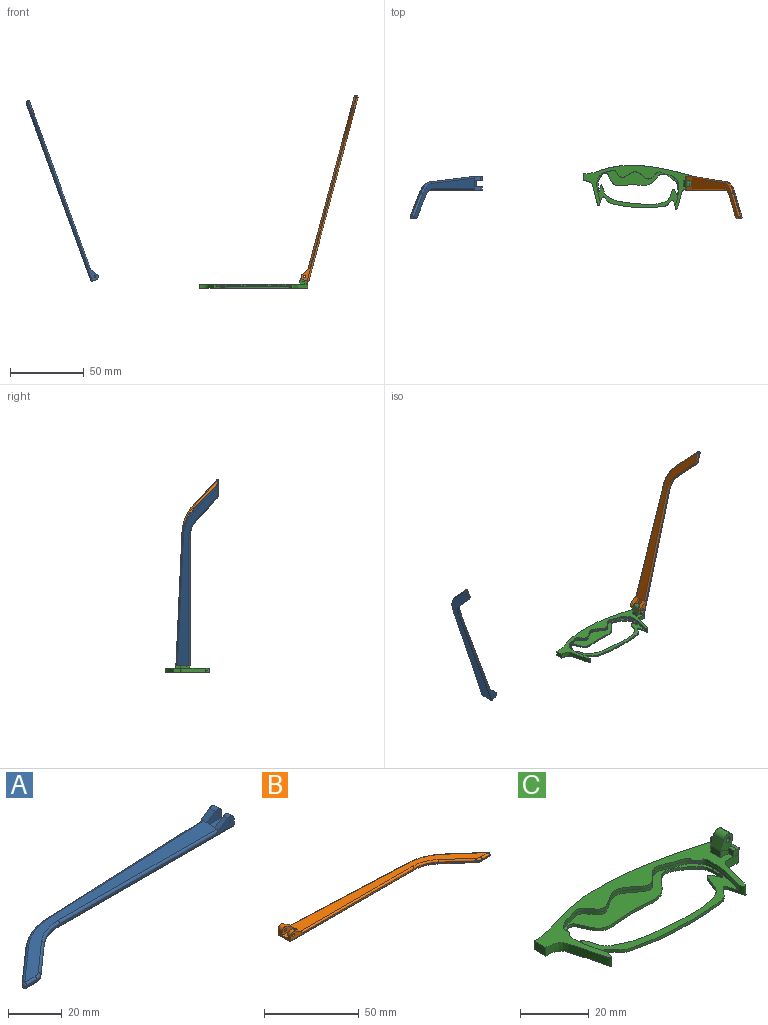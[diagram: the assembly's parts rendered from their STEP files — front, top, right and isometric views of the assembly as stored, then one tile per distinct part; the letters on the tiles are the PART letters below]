
ASSEMBLY  parts=3 mates=1
PART A: 43 faces, bbox 130.2x29.5x5.9 mm
  f0: plane 9.62x3.72mm, normal (1,0,0), area 24.7mm2, adj f1,f3,f4,f5,f10,f16,f18,f28
  f1: cylinder r=2.2mm len=3.45mm, axis (0,-1,0), area 11mm2, adj f0,f2,f4,f37
  f2: plane 6.01x3.91mm, normal (-0.55,0,0.84), area 12.7mm2, adj f1,f4,f9,f19,f37
  f3: plane 2.26x0.1mm, normal (0,0,1), area 0.1mm2, adj f0,f5,f18
  f4: plane 92.1x4.9mm, normal (0,-1,0), area 79.9mm2, adj f0,f1,f2,f14,f19,f36,f42
  f5: plane 93.42x4.13mm, normal (-0.04,1,0), area 64.8mm2, adj f0,f3,f11,f15,f17,f27,f28
  f6: plane 17.82x15.72mm, normal (-0.66,0.75,0), area 14.3mm2, adj f11,f12,f25,f30
  f7: plane 5.46x0.6mm, normal (0,-1,0), area 3.3mm2, adj f12,f13,f23,f32
  f8: plane 14.99x13.23mm, normal (0.66,-0.75,0), area 12mm2, adj f13,f14,f21,f34
  f9: plane 121.18x26.73mm, normal (0,0,1), area 627.7mm2, adj f2,f17,f19,f20,f21,f22,f23,f25
  f10: plane 129.1x27.08mm, normal (0,0,-1), area 686.5mm2, adj f0,f28,f29,f30,f32,f33,f34,f35
  f11: cylinder r=30mm len=18.52mm, axis (0,0,-1), area 12.2mm2, adj f5,f6,f26,f29
  f12: cylinder r=1mm len=1.75mm, axis (0,0,-1), area 1.5mm2, adj f6,f7,f24,f31
  f13: cylinder r=5mm len=3.31mm, axis (0,0,-1), area 2.2mm2, adj f7,f8,f22,f33
  f14: cylinder r=20mm len=13.23mm, axis (0,0,1), area 8.7mm2, adj f4,f8,f20,f35
  f15: plane 5.66x0.25mm, normal (0,0,-1), area 0.7mm2, adj f5,f17,f18
  f16: cylinder r=2.2mm len=3.45mm, axis (0,-1,0), area 14.8mm2, adj f0,f17,f18,f38
  f17: plane 6.01x3.91mm, normal (-0.55,0,0.84), area 16.9mm2, adj f5,f9,f15,f16,f18,f27,f38
  f18: plane 7.92x3.3mm, normal (0,1,0), area 15.9mm2, adj f0,f3,f15,f16,f17,f41
  f19: cylinder r=1mm len=84.18mm, axis (-1,0,0), area 131.4mm2, adj f2,f4,f9,f20
  f20: torus R=21mm, axis (0,0,1), area 23.1mm2, adj f9,f14,f19,f21
  f21: cylinder r=1mm len=15.65mm, axis (-0.75,-0.66,0), area 31.4mm2, adj f8,f9,f20,f22
  f22: torus R=4mm, axis (0,0,1), area 5.3mm2, adj f9,f13,f21,f23
  f23: cylinder r=1mm len=5.46mm, axis (-1,0,0), area 8.6mm2, adj f7,f9,f22,f24
  f24: sphere r=1mm, area 2.4mm2, adj f12,f23,f25
  f25: cylinder r=1mm len=18.48mm, axis (0.75,0.66,0), area 37.3mm2, adj f6,f9,f24,f26
  f26: torus R=29mm, axis (0,0,1), area 31.6mm2, adj f9,f11,f25,f27
  f27: cylinder r=1mm len=85.5mm, axis (1,0.04,0), area 133.5mm2, adj f5,f9,f17,f26
  f28: cylinder r=1mm len=93.46mm, axis (-1,-0.04,0), area 146.9mm2, adj f0,f5,f10,f29
  f29: torus R=29mm, axis (0,0,1), area 31.6mm2, adj f10,f11,f28,f30
  f30: cylinder r=1mm len=18.48mm, axis (-0.75,-0.66,0), area 37.3mm2, adj f6,f10,f29,f31
  f31: sphere r=1mm, area 2.4mm2, adj f12,f30,f32
  f32: cylinder r=1mm len=5.46mm, axis (1,0,0), area 8.6mm2, adj f7,f10,f31,f33
  f33: torus R=4mm, axis (0,0,1), area 5.3mm2, adj f10,f13,f32,f34
  f34: cylinder r=1mm len=15.65mm, axis (0.75,0.66,0), area 31.4mm2, adj f8,f10,f33,f35
  f35: torus R=21mm, axis (0,0,1), area 23.1mm2, adj f10,f14,f34,f36
  f36: cylinder r=1mm len=92.1mm, axis (1,0,0), area 144.7mm2, adj f0,f4,f10,f35
  f37: plane 7.92x4.7mm, normal (0,1,0), area 27mm2, adj f0,f1,f2,f39,f40,f42
  f38: plane 7.92x4.7mm, normal (0,-1,0), area 27mm2, adj f0,f16,f17,f39,f40,f41
  f39: plane 7.92x4.1mm, normal (0,0,1), area 32.5mm2, adj f0,f37,f38,f40
  f40: plane 4.1x1.4mm, normal (1,0,0), area 5.7mm2, adj f9,f37,f38,f39
  f41: cylinder r=0.5mm len=3.1mm, axis (0,-1,0), area 9.7mm2, adj f18,f38
  f42: cylinder r=0.5mm len=2.3mm, axis (0,-1,0), area 7.2mm2, adj f4,f37
PART B: 43 faces, bbox 130.2x29.5x5.9 mm
  f0: plane 9.62x3.72mm, normal (-1,0,0), area 24.7mm2, adj f1,f3,f4,f5,f10,f16,f18,f28
  f1: cylinder r=2.2mm len=3.45mm, axis (0,-1,0), area 11mm2, adj f0,f2,f4,f37
  f2: plane 6.01x3.91mm, normal (0.55,0,0.84), area 12.7mm2, adj f1,f4,f9,f19,f37
  f3: plane 2.26x0.1mm, normal (0,0,1), area 0.1mm2, adj f0,f5,f18
  f4: plane 92.1x4.9mm, normal (0,-1,0), area 78.2mm2, adj f0,f1,f2,f14,f19,f36,f42
  f5: plane 93.42x4.13mm, normal (0.04,1,0), area 64.8mm2, adj f0,f3,f11,f15,f17,f27,f28
  f6: plane 17.82x15.72mm, normal (0.66,0.75,0), area 14.3mm2, adj f11,f12,f25,f30
  f7: plane 5.46x0.6mm, normal (0,-1,0), area 3.3mm2, adj f12,f13,f23,f32
  f8: plane 14.99x13.23mm, normal (-0.66,-0.75,0), area 12mm2, adj f13,f14,f21,f34
  f9: plane 121.18x26.73mm, normal (0,0,1), area 627.7mm2, adj f2,f17,f19,f20,f21,f22,f23,f25
  f10: plane 129.1x27.08mm, normal (0,0,-1), area 686.5mm2, adj f0,f28,f29,f30,f32,f33,f34,f35
  f11: cylinder r=30mm len=18.52mm, axis (0,0,-1), area 12.2mm2, adj f5,f6,f26,f29
  f12: cylinder r=1mm len=1.75mm, axis (0,0,-1), area 1.5mm2, adj f6,f7,f24,f31
  f13: cylinder r=5mm len=3.31mm, axis (0,0,-1), area 2.2mm2, adj f7,f8,f22,f33
  f14: cylinder r=20mm len=13.23mm, axis (0,0,1), area 8.7mm2, adj f4,f8,f20,f35
  f15: plane 5.66x0.25mm, normal (0,0,-1), area 0.7mm2, adj f5,f17,f18
  f16: cylinder r=2.2mm len=3.45mm, axis (0,-1,0), area 14.8mm2, adj f0,f17,f18,f38
  f17: plane 6.01x3.91mm, normal (0.55,0,0.84), area 16.9mm2, adj f5,f9,f15,f16,f18,f27,f38
  f18: plane 7.92x3.3mm, normal (0,1,0), area 14.3mm2, adj f0,f3,f15,f16,f17,f41
  f19: cylinder r=1mm len=84.18mm, axis (1,0,0), area 131.4mm2, adj f2,f4,f9,f20
  f20: torus R=21mm, axis (0,0,1), area 23.1mm2, adj f9,f14,f19,f21
  f21: cylinder r=1mm len=15.65mm, axis (0.75,-0.66,0), area 31.4mm2, adj f8,f9,f20,f22
  f22: torus R=4mm, axis (0,0,1), area 5.3mm2, adj f9,f13,f21,f23
  f23: cylinder r=1mm len=5.46mm, axis (1,0,0), area 8.6mm2, adj f7,f9,f22,f24
  f24: sphere r=1mm, area 2.4mm2, adj f12,f23,f25
  f25: cylinder r=1mm len=18.48mm, axis (-0.75,0.66,0), area 37.3mm2, adj f6,f9,f24,f26
  f26: torus R=29mm, axis (0,0,1), area 31.6mm2, adj f9,f11,f25,f27
  f27: cylinder r=1mm len=85.5mm, axis (-1,0.04,0), area 133.5mm2, adj f5,f9,f17,f26
  f28: cylinder r=1mm len=93.46mm, axis (1,-0.04,0), area 146.9mm2, adj f0,f5,f10,f29
  f29: torus R=29mm, axis (0,0,1), area 31.6mm2, adj f10,f11,f28,f30
  f30: cylinder r=1mm len=18.48mm, axis (0.75,-0.66,0), area 37.3mm2, adj f6,f10,f29,f31
  f31: sphere r=1mm, area 2.4mm2, adj f12,f30,f32
  f32: cylinder r=1mm len=5.46mm, axis (-1,0,0), area 8.6mm2, adj f7,f10,f31,f33
  f33: torus R=4mm, axis (0,0,1), area 5.3mm2, adj f10,f13,f32,f34
  f34: cylinder r=1mm len=15.65mm, axis (-0.75,0.66,0), area 31.4mm2, adj f8,f10,f33,f35
  f35: torus R=21mm, axis (0,0,1), area 23.1mm2, adj f10,f14,f34,f36
  f36: cylinder r=1mm len=92.1mm, axis (-1,0,0), area 144.7mm2, adj f0,f4,f10,f35
  f37: plane 7.92x4.7mm, normal (0,1,0), area 25.4mm2, adj f0,f1,f2,f39,f40,f42
  f38: plane 7.92x4.7mm, normal (0,-1,0), area 25.4mm2, adj f0,f16,f17,f39,f40,f41
  f39: plane 7.92x4.1mm, normal (0,0,1), area 32.5mm2, adj f0,f37,f38,f40
  f40: plane 4.1x1.4mm, normal (-1,0,0), area 5.7mm2, adj f9,f37,f38,f39
  f41: cylinder r=0.88mm len=3.1mm, axis (0,-1,0), area 17mm2, adj f18,f38
  f42: cylinder r=0.88mm len=2.3mm, axis (0,-1,0), area 12.6mm2, adj f4,f37
PART C: 34 faces, bbox 74.2x30.9x10.4 mm
  f0: plane 1.26x0.04mm, normal (0,0,1), area 0mm2, adj f3,f5,f14
  f1: plane 6.97x5.07mm, normal (0,1,0), area 22.7mm2, adj f3,f12,f13,f17,f19,f20,f22,f23
  f2: plane 3.2x2.36mm, normal (0,-1,0), area 5.7mm2, adj f3,f12,f18,f21
  f3: plane 73.77x30.65mm, normal (0,0,1), area 447.4mm2, adj f0,f1,f2,f5,f6,f7,f11,f12
  f4: extruded ~54.23x21.06mm, area 148.7mm2, adj f8,f9
  f5: extruded ~73.3x29.33mm, area 316.5mm2, adj f0,f3,f6,f7,f8,f9,f10,f11
  f6: extruded ~35.39x5.69mm, area 108.2mm2, adj f3,f5,f7,f8
  f7: plane 4.79x3mm, normal (-1,0,0), area 14.4mm2, adj f3,f5,f6,f8
  f8: plane 73.62x30.5mm, normal (0,0,-1), area 913.1mm2, adj f4,f5,f6,f7
  f9: plane 56.11x25.94mm, normal (0,0,1), area 422.1mm2, adj f4,f5,f10
  f10: extruded ~55.74x24.27mm, area 99.2mm2, adj f5,f9,f11
  f11: extruded ~55.74x24.27mm, area 96.1mm2, adj f3,f5,f10,f29,f30,f31,f32
  f12: plane 4x2.36mm, normal (-1,0,0), area 9.5mm2, adj f1,f2,f3,f13
  f13: plane 4x0.02mm, normal (0.34,0,0.94), area 0.1mm2, adj f1,f12,f20
  f14: plane 2.73x2.49mm, normal (0,-1,0), area 3.9mm2, adj f0,f18,f19,f27,f33
  f15: plane 7.66x1.6mm, normal (0.94,0,-0.34), area 13mm2, adj f3,f27,f28,f33
  f16: plane 2.1x1.68mm, normal (0,1,0), area 2.8mm2, adj f3,f17,f19,f28,f33
  f17: plane 3.3x2.1mm, normal (-1,0,0), area 6.9mm2, adj f1,f3,f16,f19
  f18: plane 2.34x2.1mm, normal (-1,0,0), area 4.9mm2, adj f2,f3,f14,f19,f21
  f19: plane 9.64x1.24mm, normal (0,0,1), area 8.2mm2, adj f1,f14,f16,f17,f18,f21,f22,f33
  f20: plane 4x3.31mm, normal (-0.94,0,0.34), area 14.1mm2, adj f1,f13,f21,f24
  f21: plane 5.77x5.06mm, normal (0,-1,0), area 17mm2, adj f2,f18,f19,f20,f22,f23,f24,f25
  f22: plane 4x2.21mm, normal (0.94,0,-0.34), area 9.4mm2, adj f1,f19,f21,f25
  f23: plane 4x0.01mm, normal (0.34,0,0.94), area 0mm2, adj f1,f21,f24,f25
  f24: cylinder r=1.98mm len=4mm, axis (0,1,0), area 12.4mm2, adj f1,f20,f21,f23
  f25: cylinder r=1.98mm len=4mm, axis (0,-1,0), area 12.4mm2, adj f1,f21,f22,f23
  f26: cylinder r=0.88mm len=4mm, axis (0,-1,0), area 22mm2, adj f1,f21
  f27: cone r=1mm half-angle=20deg, axis (0,0,1), area 2.3mm2, adj f3,f14,f15,f33
  f28: cylinder r=1mm len=2.28mm, axis (-0.34,0,-0.94), area 3mm2, adj f3,f15,f16,f33
  f29: plane 3.19x1.37mm, normal (0,0,-1), area 2.1mm2, adj f11,f30
  f30: cylinder r=2.28mm len=3.17mm, axis (0,0,1), area 1.9mm2, adj f3,f11,f29
  f31: plane 3.14x2.79mm, normal (0,0,-1), area 3.9mm2, adj f11,f32
  f32: cylinder r=2.28mm len=3.13mm, axis (0,0,1), area 2.5mm2, adj f3,f11,f31
  f33: plane 9.69x1.44mm, normal (0.34,0,0.94), area 13.9mm2, adj f14,f15,f16,f19,f27,f28
PLACE A rot(axis=(0,1,0),70deg) t=(-84.77,-5.75,56)mm
PLACE B rot(axis=(0,-1,0),75deg) t=(68.2,-5.75,-61.61)mm
PLACE C t=(10.15,-1.13,-5.77)mm
MATE revolute B.f41 <-> C.f25  axis (0,-1,0) through (81.2,2.72,1.21)mm
